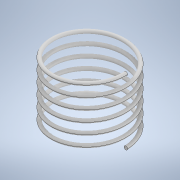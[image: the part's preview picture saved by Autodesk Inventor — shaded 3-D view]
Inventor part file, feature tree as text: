
AUTODESK INVENTOR PART (.ipt)
format: ipt  version: 2020 (Build 240168000, 168)  size: 265,216 bytes
history: native  units: mm
features: helix x1, sketch x1
ambient origin geometry x8: Origin, YZ Plane, XZ Plane, XY Plane, X Axis, Y Axis, Z Axis, Center Point
bodies: Solid1 (feature_tree)
feature tree (2):
  helix  "Coil1"  [1 undecoded]
  sketch  "Sketch1"  dims[d1=1.0mm d2=3.0mm d3=18.0mm d4=10.0mm d5=0.0mm d6=90.0deg d7=90.0deg d8=0.0mm d9=0.0mm]
note: 1 required parameter value undecoded (feature->parameter linkage not recoverable at this tier; creation-order binding heuristic only, values carry confidence <= 0.55)
